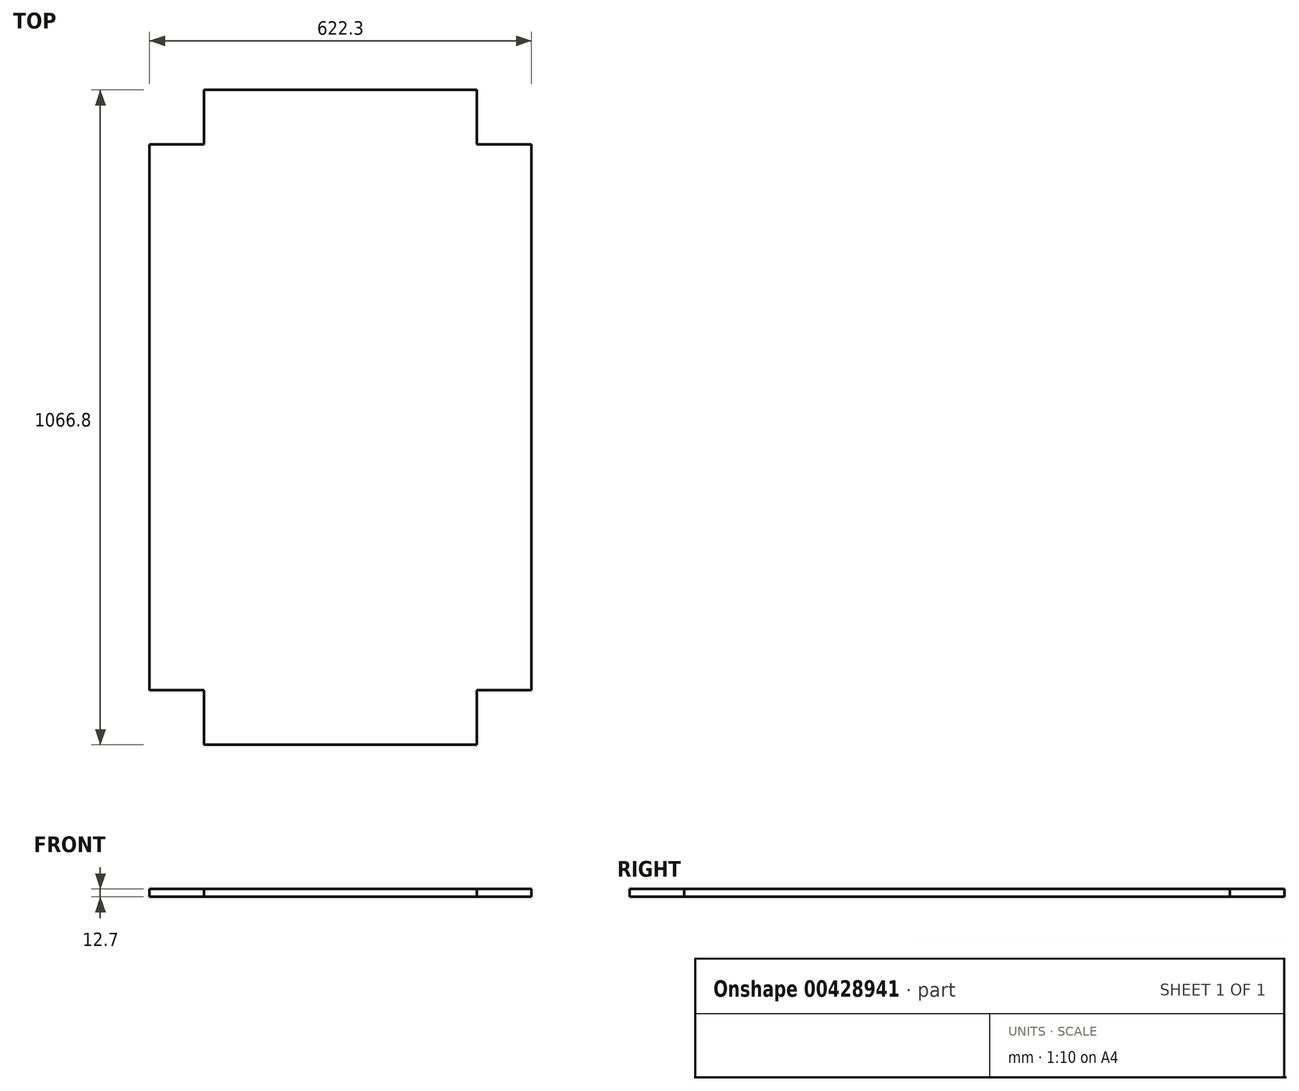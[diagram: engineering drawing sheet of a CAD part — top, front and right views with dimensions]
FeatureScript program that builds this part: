
annotation { "Feature Type Name" : "Feature", "Feature Type Description" : "" }
export const myFeature = defineFeature(function(context is Context, id is Id, definition is map)
    precondition{}
    {
        {
            var Q0;
            Q0=qCreatedBy(makeId("Top.planeOp"),FACE);
            var sketch = newSketch(context, id + "F0", { "sketchPlane" : qUnion([Q0])});
            skLineSegment(sketch, "E0.bottom", {"start": v(410.96, -59.08) * mm, "end": v(-33.54, -59.08) * mm});
            skLineSegment(sketch, "E0.top", {"start": v(410.96, 1007.72) * mm, "end": v(-33.54, 1007.72) * mm});
            skLineSegment(sketch, "E0.left", {"start": v(499.86, 29.82) * mm, "end": v(499.86, 918.82) * mm});
            skLineSegment(sketch, "E0.right", {"start": v(-122.44, 29.82) * mm, "end": v(-122.44, 918.82) * mm});
            skLineSegment(sketch, "E1.top", {"start": v(-122.44, 918.82) * mm, "end": v(-33.54, 918.82) * mm});
            skLineSegment(sketch, "E1.right", {"start": v(-33.54, 1007.72) * mm, "end": v(-33.54, 918.82) * mm});
            skLineSegment(sketch, "E2.top", {"start": v(499.86, 918.82) * mm, "end": v(410.96, 918.82) * mm});
            skLineSegment(sketch, "E2.right", {"start": v(410.96, 1007.72) * mm, "end": v(410.96, 918.82) * mm});
            skLineSegment(sketch, "E3.top", {"start": v(499.86, 29.82) * mm, "end": v(410.96, 29.82) * mm});
            skLineSegment(sketch, "E3.right", {"start": v(410.96, -59.08) * mm, "end": v(410.96, 29.82) * mm});
            skLineSegment(sketch, "E4.top", {"start": v(-122.44, 29.82) * mm, "end": v(-33.54, 29.82) * mm});
            skLineSegment(sketch, "E4.right", {"start": v(-33.54, -59.08) * mm, "end": v(-33.54, 29.82) * mm});
            skSolve(sketch);
        }
        {
            var Q0;
            Q0=makeQuery(id+"F0.imprint","IMPRINT",FACE,{"disambiguationData":[TD([[makeQuery(id+"F0.imprint","IMPRINT",EDGE,{"derivedFrom":sQuery(id+"F0.wireOp",EDGE,"E0.bottom")}),-1.0]])]});
            extrude(context, id + "F1", {"entities" : qUnion([Q0]), "depth" : 12.7 * mm});
        }
    });
